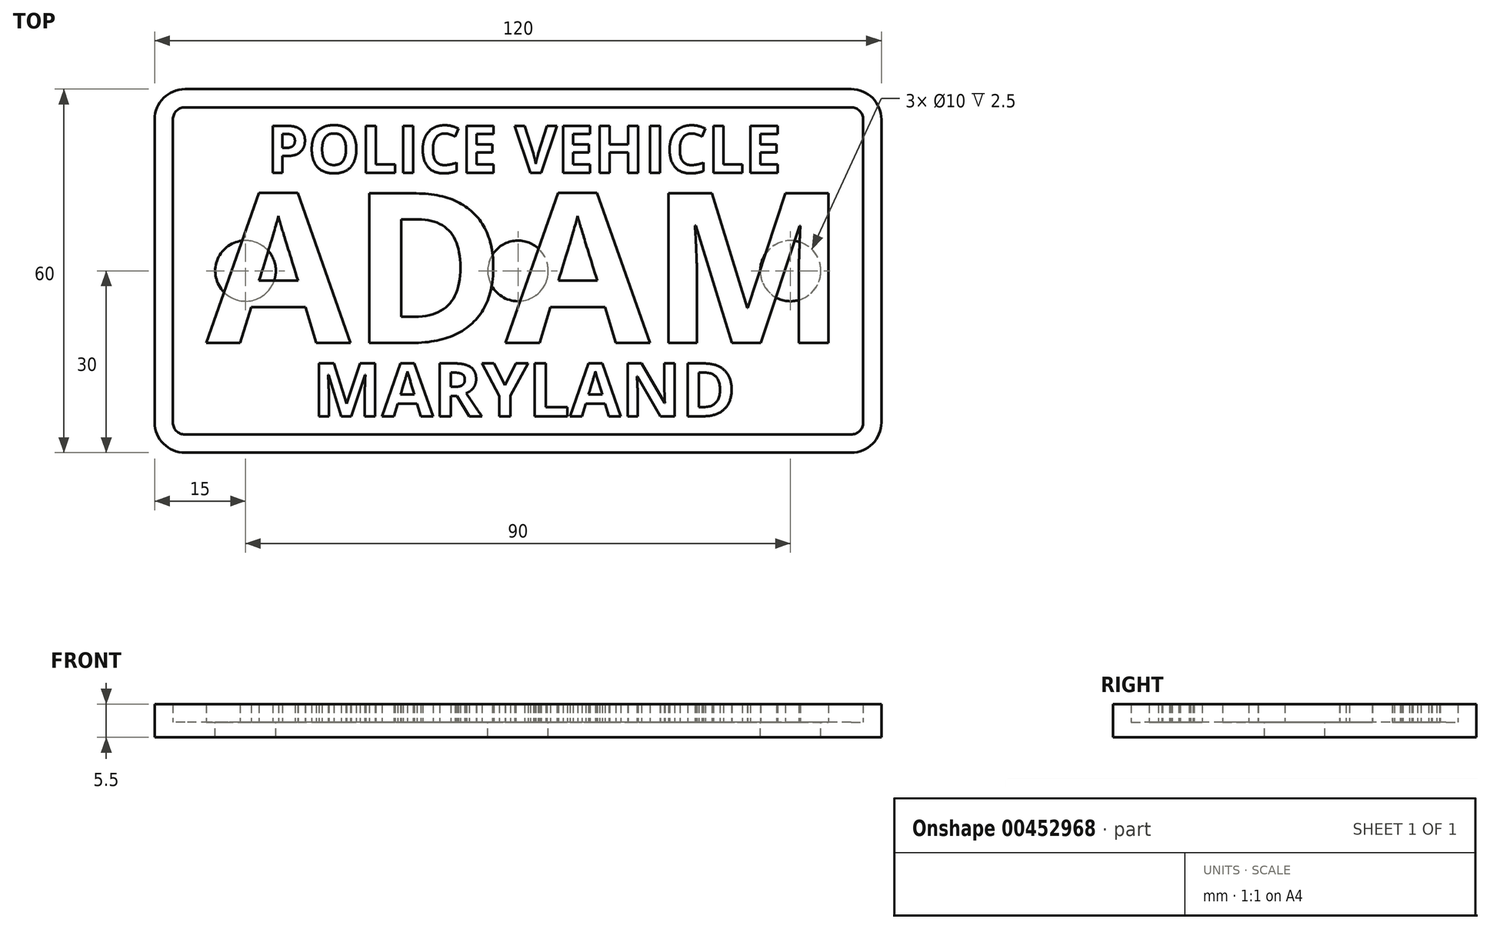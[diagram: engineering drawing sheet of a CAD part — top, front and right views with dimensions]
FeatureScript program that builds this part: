
annotation { "Feature Type Name" : "Feature", "Feature Type Description" : "" }
export const myFeature = defineFeature(function(context is Context, id is Id, definition is map)
    precondition{}
    {
        {
            var Q0;
            Q0=qCreatedBy(makeId("Top.planeOp"),FACE);
            var sketch = newSketch(context, id + "F0", { "sketchPlane" : qUnion([Q0])});
            skLineSegment(sketch, "E0.bottom", {"start": v(60, -30) * mm, "end": v(-60, -30) * mm});
            skLineSegment(sketch, "E0.top", {"start": v(60, 30) * mm, "end": v(-60, 30) * mm});
            skLineSegment(sketch, "E0.left", {"start": v(60, -30) * mm, "end": v(60, 30) * mm});
            skLineSegment(sketch, "E0.right", {"start": v(-60, -30) * mm, "end": v(-60, 30) * mm});
            skPoint(sketch, "E0.middle", {"position": v(0, 0) * mm});
            skSolve(sketch);
        }
        {
            var Q0;
            Q0=qCreatedBy(makeId("Top.planeOp"),FACE);
            cPlane(context, id + "F1", {"entities" : qUnion([Q0]), "cplaneType" : CPlaneType.OFFSET, "offset" : 2.5 * mm, "width" : 150 * mm, "height" : 150 * mm});
        }
        {
            var Q0;
            Q0 = qSketchRegion(id + "F0", true);
            extrude(context, id + "F2", {"entities" : qUnion([Q0]), "depth" : 2.5 * mm, "offsetDistance" : 25 * mm});
        }
        {
            var Q0;
            Q0=qCreatedBy(id+"F1.planeOp",FACE);
            var sketch = newSketch(context, id + "F3", { "sketchPlane" : qUnion([Q0])});
            skCircle(sketch, "E1", {"center": v(0, 0) * mm, "radius": 5 * mm});
            skCircle(sketch, "E2", {"center": v(-45, 0) * mm, "radius": 5 * mm});
            skCircle(sketch, "E3.MirrorC", {"center": v(45, 0) * mm, "radius": 5 * mm});
            skSolve(sketch);
        }
        {
            var Q0;
            Q0 = qSketchRegion(id + "F3", true);
            extrude(context, id + "F4", {"entities" : qUnion([Q0]), "operationType" : NewBodyOperationType.REMOVE, "oppositeDirection" : true, "depth" : 2.5 * mm, "offsetDistance" : 25 * mm});
        }
        {
            var Q0;
            Q0=qCreatedBy(id+"F1.planeOp",FACE);
            var sketch = newSketch(context, id + "F5", { "sketchPlane" : qUnion([Q0])});
            skText(sketch, "E4", { "text": "ADAM", "fontName": "OpenSans-Bold.ttf"});
            skText(sketch, "E5", { "text": "MARYLAND", "fontName": "OpenSans-Bold.ttf"});
            skText(sketch, "E6", { "text": "POLICE VEHICLE\n", "fontName": "OpenSans-Bold.ttf"});
            skPoint(sketch, "E7.middle", {"position": v(0, 0) * mm});
            const initialGuessF5  = {"E4": [-0.0515, -0.01188, 1, 0, 0.02488], "E5": [-0.034, -0.024, 1, 0, 0.0088], "E6": [-0.0415, 0.0162, 1, 0, 0.0078]};
            skSetInitialGuess(sketch, initialGuessF5);
            skSolve(sketch);
        }
        {
            var Q0;
            Q0 = qSketchRegion(id + "F5", true);
            extrude(context, id + "F6", {"entities" : qUnion([Q0]), "operationType" : NewBodyOperationType.ADD, "depth" : 3 * mm, "offsetDistance" : 25 * mm});
        }
        {
            var Q0;
            {var subQ25=sQuery(id+"F0.wireOp",EDGE,"E0.bottom");var subQ37=sQuery(id+"F0.wireOp",EDGE,"E0.top");var subQ41=sQuery(id+"F0.wireOp",EDGE,"E0.left");var subQ42=sQuery(id+"F0.wireOp",EDGE,"E0.right");Q0=makeQuery(id+"F6.boolean.opBoolean","SPLIT",FACE,{"disambiguationData":[TD([makeQuery(id+"F2.opExtrude","SWEPT_FACE",FACE,{"disambiguationData":[OSD([subQ25])]})])],"derivedFrom":makeQuery(id+"F2.opExtrude","CAP_FACE",FACE,{"disambiguationData":[OSD([subQ25,subQ37,subQ41,subQ42])],"isStart":false})});}
            var sketch = newSketch(context, id + "F7", { "sketchPlane" : qUnion([Q0])});
            skLineSegment(sketch, "E8.bottom", {"start": v(60, 30) * mm, "end": v(-60, 30) * mm});
            skLineSegment(sketch, "E8.top", {"start": v(60, -30) * mm, "end": v(-60, -30) * mm});
            skLineSegment(sketch, "E8.left", {"start": v(60, 30) * mm, "end": v(60, -30) * mm});
            skLineSegment(sketch, "E8.right", {"start": v(-60, 30) * mm, "end": v(-60, -30) * mm});
            skPoint(sketch, "E8.middle", {"position": v(0, 0) * mm});
            skLineSegment(sketch, "E9.bottom", {"start": v(57, 27) * mm, "end": v(-57, 27) * mm});
            skLineSegment(sketch, "E9.top", {"start": v(57, -27) * mm, "end": v(-57, -27) * mm});
            skLineSegment(sketch, "E9.left", {"start": v(57, 27) * mm, "end": v(57, -27) * mm});
            skLineSegment(sketch, "E9.right", {"start": v(-57, 27) * mm, "end": v(-57, -27) * mm});
            skSolve(sketch);
        }
        {
            var Q0;
            Q0 = qSketchRegion(id + "F7", true);
            extrude(context, id + "F8", {"entities" : qUnion([Q0]), "operationType" : NewBodyOperationType.ADD, "depth" : 3 * mm, "offsetDistance" : 25 * mm});
        }
        {
            var Q0;
            Q0=makeQuery(id+"F8.boolean.opBoolean","MERGE",EDGE,{"derivedFrom":[makeQuery(id+"F2.opExtrude","SWEPT_EDGE",EDGE,{"disambiguationData":[OSD([sQuery(id+"F0.wireOp",EDGE,"E0.bottom"),sQuery(id+"F0.wireOp",EDGE,"E0.left")])]}),makeQuery(id+"F8.opExtrude","SWEPT_EDGE",EDGE,{"disambiguationData":[OSD([sQuery(id+"F7.wireOp",EDGE,"E8.top"),sQuery(id+"F7.wireOp",EDGE,"E8.left")])]})]});
            var Q1;
            Q1=makeQuery(id+"F8.boolean.opBoolean","MERGE",EDGE,{"derivedFrom":[makeQuery(id+"F2.opExtrude","SWEPT_EDGE",EDGE,{"disambiguationData":[OSD([sQuery(id+"F0.wireOp",EDGE,"E0.top"),sQuery(id+"F0.wireOp",EDGE,"E0.left")])]}),makeQuery(id+"F8.opExtrude","SWEPT_EDGE",EDGE,{"disambiguationData":[OSD([sQuery(id+"F7.wireOp",EDGE,"E8.bottom"),sQuery(id+"F7.wireOp",EDGE,"E8.left")])]})]});
            var Q2;
            Q2=makeQuery(id+"F8.boolean.opBoolean","MERGE",EDGE,{"derivedFrom":[makeQuery(id+"F2.opExtrude","SWEPT_EDGE",EDGE,{"disambiguationData":[OSD([sQuery(id+"F0.wireOp",EDGE,"E0.top"),sQuery(id+"F0.wireOp",EDGE,"E0.right")])]}),makeQuery(id+"F8.opExtrude","SWEPT_EDGE",EDGE,{"disambiguationData":[OSD([sQuery(id+"F7.wireOp",EDGE,"E8.bottom"),sQuery(id+"F7.wireOp",EDGE,"E8.right")])]})]});
            var Q3;
            Q3=makeQuery(id+"F8.boolean.opBoolean","MERGE",EDGE,{"derivedFrom":[makeQuery(id+"F2.opExtrude","SWEPT_EDGE",EDGE,{"disambiguationData":[OSD([sQuery(id+"F0.wireOp",EDGE,"E0.bottom"),sQuery(id+"F0.wireOp",EDGE,"E0.right")])]}),makeQuery(id+"F8.opExtrude","SWEPT_EDGE",EDGE,{"disambiguationData":[OSD([sQuery(id+"F7.wireOp",EDGE,"E8.top"),sQuery(id+"F7.wireOp",EDGE,"E8.right")])]})]});
            fillet(context, id + "F9", {"entities" : qUnion([Q0, Q1, Q2, Q3]), "radius" : 5 * mm, "tangentPropagation" : true, "allowEdgeOverflow" : false});
        }
        {
            var Q0;
            Q0=makeQuery(id+"F8.opExtrude","SWEPT_EDGE",EDGE,{"disambiguationData":[OSD([sQuery(id+"F7.wireOp",EDGE,"E9.top"),sQuery(id+"F7.wireOp",EDGE,"E9.right")])]});
            var Q1;
            Q1=makeQuery(id+"F8.opExtrude","SWEPT_EDGE",EDGE,{"disambiguationData":[OSD([sQuery(id+"F7.wireOp",EDGE,"E9.bottom"),sQuery(id+"F7.wireOp",EDGE,"E9.right")])]});
            var Q2;
            Q2=makeQuery(id+"F8.opExtrude","SWEPT_EDGE",EDGE,{"disambiguationData":[OSD([sQuery(id+"F7.wireOp",EDGE,"E9.bottom"),sQuery(id+"F7.wireOp",EDGE,"E9.left")])]});
            var Q3;
            Q3=makeQuery(id+"F8.opExtrude","SWEPT_EDGE",EDGE,{"disambiguationData":[OSD([sQuery(id+"F7.wireOp",EDGE,"E9.top"),sQuery(id+"F7.wireOp",EDGE,"E9.left")])]});
            fillet(context, id + "F10", {"entities" : qUnion([Q0, Q1, Q2, Q3]), "radius" : 2 * mm, "tangentPropagation" : true, "allowEdgeOverflow" : false});
        }
    });
